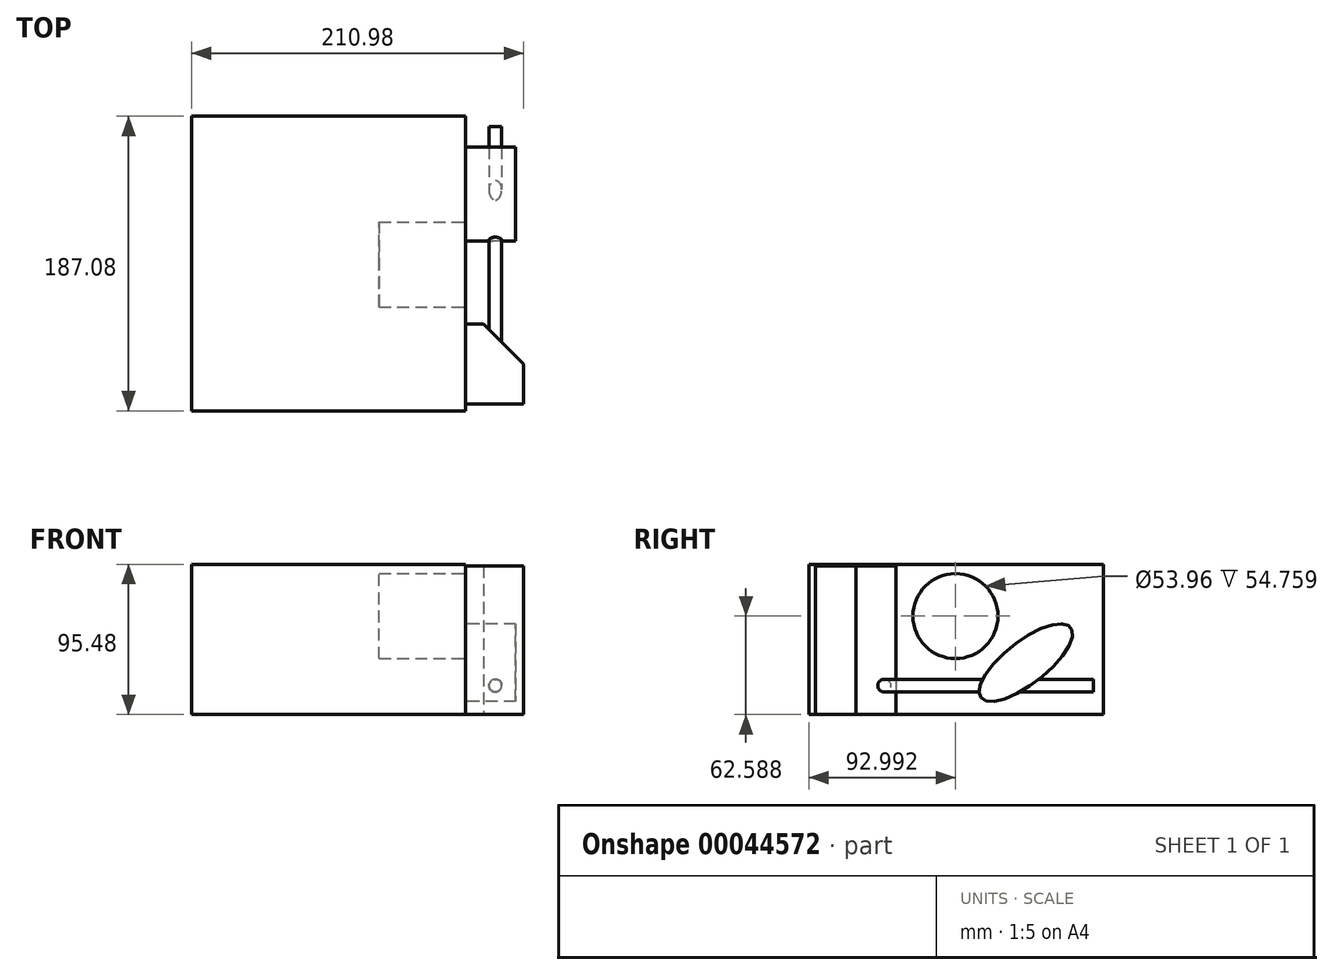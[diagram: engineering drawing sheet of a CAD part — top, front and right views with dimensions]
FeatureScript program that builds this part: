
annotation { "Feature Type Name" : "Feature", "Feature Type Description" : "" }
export const myFeature = defineFeature(function(context is Context, id is Id, definition is map)
    precondition{}
    {
        {
            var Q0;
            Q0=qCreatedBy(makeId("Top.planeOp"),FACE);
            var sketch = newSketch(context, id + "F0", { "sketchPlane" : qUnion([Q0])});
            skLineSegment(sketch, "E0.bottom", {"start": v(-89.4, -42.52) * mm, "end": v(84.52, -42.52) * mm});
            skLineSegment(sketch, "E0.top", {"start": v(-89.4, 144.56) * mm, "end": v(84.52, 144.56) * mm});
            skLineSegment(sketch, "E0.left", {"start": v(-89.4, -42.52) * mm, "end": v(-89.4, 144.56) * mm});
            skLineSegment(sketch, "E0.right", {"start": v(84.52, -42.52) * mm, "end": v(84.52, 144.56) * mm});
            skSolve(sketch);
        }
        {
            var Q0;
            Q0 = qSketchRegion(id + "F0", true);
            extrude(context, id + "F1", {"entities" : qUnion([Q0]), "depth" : 95.48 * mm});
        }
        {
            var Q0;
            Q0=makeQuery(id+"F1.opExtrude","SWEPT_FACE",FACE,{"disambiguationData":[OSD([sQuery(id+"F0.wireOp",EDGE,"E0.right")])]});
            var sketch = newSketch(context, id + "F2", { "sketchPlane" : qUnion([Q0])});
            skEllipse(sketch, "E1", {"center": v(95.16, 33.06) * mm, "majorRadius": 36.19 * mm, "minorRadius": 13.52 * mm, "majorAxis": v(-0.79, -0.61)});
            skSolve(sketch);
        }
        {
            var Q0;
            Q0=makeQuery(id+"F2.imprint","IMPRINT",FACE,{"disambiguationData":[TD([[makeQuery(id+"F2.imprint","IMPRINT",EDGE,{"derivedFrom":sQuery(id+"F2.wireOp",EDGE,"E1")}),1.0]])]});
            extrude(context, id + "F3", {"entities" : qUnion([Q0]), "operationType" : NewBodyOperationType.ADD, "depth" : 31.9 * mm});
        }
        {
            var Q0;
            Q0=makeQuery(id+"F2.imprint","IMPRINT",FACE,{"disambiguationData":[TD([[makeQuery(id+"F2.imprint","IMPRINT",EDGE,{"derivedFrom":sQuery(id+"F2.wireOp",EDGE,"E1")}),-1.0]])]});
            var sketch = newSketch(context, id + "F4", { "sketchPlane" : qUnion([Q0])});
            skCircle(sketch, "E2", {"center": v(4.57, 31.29) * mm, "radius": 16.24 * mm});
            skCircle(sketch, "E3", {"center": v(50.47, 62.59) * mm, "radius": 26.98 * mm});
            skSolve(sketch);
        }
        {
            var Q0;
            Q0=makeQuery(id+"F4.imprint","IMPRINT",FACE,{"disambiguationData":[TD([[makeQuery(id+"F4.imprint","IMPRINT",EDGE,{"derivedFrom":sQuery(id+"F4.wireOp",EDGE,"E3")}),1.0]])]});
            extrude(context, id + "F5", {"entities" : qUnion([Q0]), "operationType" : NewBodyOperationType.REMOVE, "oppositeDirection" : true, "depth" : 54.76 * mm});
        }
        {
            var Q0;
            Q0=makeQuery(id+"F2.imprint","IMPRINT",FACE,{"disambiguationData":[TD([[makeQuery(id+"F2.imprint","IMPRINT",EDGE,{"derivedFrom":sQuery(id+"F2.wireOp",EDGE,"E1")}),-1.0]])]});
            var sketch = newSketch(context, id + "F6", { "sketchPlane" : qUnion([Q0])});
            skLineSegment(sketch, "E4.bottom", {"start": v(-38.34, 94.47) * mm, "end": v(12.56, 94.47) * mm});
            skLineSegment(sketch, "E4.top", {"start": v(-38.34, 0) * mm, "end": v(12.56, 0) * mm});
            skLineSegment(sketch, "E4.left", {"start": v(-38.34, 94.47) * mm, "end": v(-38.34, 0) * mm});
            skLineSegment(sketch, "E4.right", {"start": v(12.56, 94.47) * mm, "end": v(12.56, 0) * mm});
            skSolve(sketch);
        }
        {
            var Q0;
            Q0 = qSketchRegion(id + "F6", true);
            extrude(context, id + "F7", {"entities" : qUnion([Q0]), "operationType" : NewBodyOperationType.ADD, "depth" : 37.06 * mm});
        }
        {
            var Q0;
            Q0=makeQuery(id+"F7.opExtrude","CAP_EDGE",EDGE,{"disambiguationData":[OSD([sQuery(id+"F6.wireOp",EDGE,"E4.right")])],"isStart":false});
            chamfer(context, id + "F8", {"entities" : qUnion([Q0]), "width" : 25.4 * mm, "tangentPropagation" : true});
        }
        {
            var Q0;
            Q0=makeQuery(id+"F7.opExtrude","SWEPT_FACE",FACE,{"disambiguationData":[OSD([sQuery(id+"F6.wireOp",EDGE,"E4.left")])]});
            var sketch = newSketch(context, id + "F9", { "sketchPlane" : qUnion([Q0])});
            skCircle(sketch, "E5", {"center": v(103.52, 18.44) * mm, "radius": 4.09 * mm});
            skSolve(sketch);
        }
        {
            var Q0;
            Q0=makeQuery(id+"F9.imprint","IMPRINT",FACE,{"disambiguationData":[TD([[makeQuery(id+"F9.imprint","IMPRINT",EDGE,{"derivedFrom":sQuery(id+"F9.wireOp",EDGE,"E5")}),1.0]])]});
            extrude(context, id + "F10", {"entities" : qUnion([Q0]), "operationType" : NewBodyOperationType.ADD, "oppositeDirection" : true, "depth" : 176.47 * mm});
        }
    });
